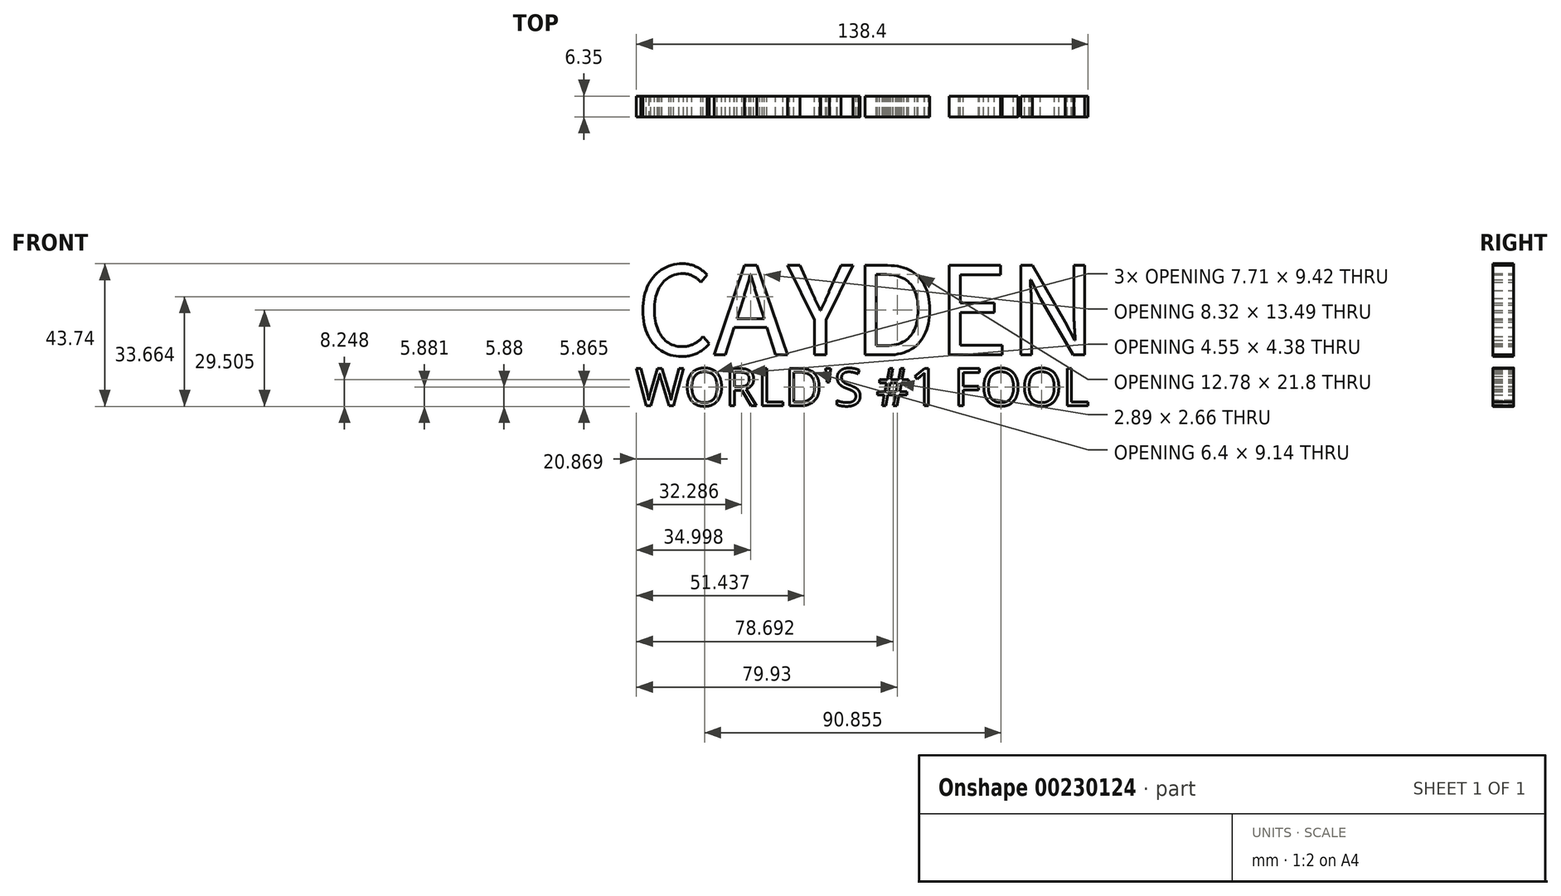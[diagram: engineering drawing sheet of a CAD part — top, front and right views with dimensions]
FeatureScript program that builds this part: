
annotation { "Feature Type Name" : "Feature", "Feature Type Description" : "" }
export const myFeature = defineFeature(function(context is Context, id is Id, definition is map)
    precondition{}
    {
        {
            var Q0;
            Q0=qCreatedBy(makeId("Front.planeOp"),FACE);
            var sketch = newSketch(context, id + "F0", { "sketchPlane" : qUnion([Q0])});
            skText(sketch, "E0", { "text": "CAYDEN", "fontName": "NotoSansCJKkr-Regular.otf"});
            skText(sketch, "E1", { "text": "WORLD\'S #1 FOOL", "fontName": "OpenSans-Regular.ttf"});
            skLineSegment(sketch, "E2", {"start": v(89.12, 34.57) * mm, "end": v(101.82, 34.57) * mm});
            skLineSegment(sketch, "E3", {"start": v(-50.58, 34.57) * mm, "end": v(-63.28, 34.57) * mm});
            const initialGuessF0  = {"E0": [-0.05058, 0.0076, 1, 0, 0.02697], "E1": [-0.05058, -0.008, 1, 0, 0.01154]};
            skSetInitialGuess(sketch, initialGuessF0);
            skSolve(sketch);
        }
        {
            var Q0;
            Q0 = qSketchRegion(id + "F0", true);
            extrude(context, id + "F1", {"entities" : qUnion([Q0]), "depth" : 6.35 * mm});
        }
    });
